# Revit family: Shower-Drain-KOHLER-Round-K-9132
name_source: partatom
category: Specialty Equipment
revit_build: Autodesk Revit 2015 (Build: 20140606_1530(x64)
units: mm (PartAtom-declared; Revit-internal decimal feet)

## types (12) — shared parameters
ADA = No
Assembly Code = C1030200
Date Modified = 02/28/2018
Default Elevation = 42"
Description = Round shower drain for use with plastic pipe, gasket included
Height = 1 15/16"
Length = 4 1/2"
Manufacturer = KOHLER Co.
MasterFormat 1995 = 10820
MasterFormat 2004 = 10.28.13
Material = Solid Brass Construction
Product Documentation Link = http://www.us.kohler.com
Product Name = Shower Drain
Product Page URL = http://www.us.kohler.com
URL = https://www.us.kohler.com
Width = 4 1/2"

## per-type parameters (varying)
| type | Finish | Model | Type |
| CP- Polished Chrome | Kohler-Metal-CP-Polished_Chrome | K-9132-CP | 1 |
| SN- Vibrant Polished Nickel | Kohler-Metal-SN-Vibrant_Polished_Nickel | K-9132-SN | 2 |
| AF- Vibrant French Gold | Kohler-Metal-AF-Vibrant_French_Gold | K-9132-AF | 3 |
| PB- Vibrant Polished Brass | Kohler-Metal-PB-Vibrant_Polished_Brass | K-9132-PB | 4 |
| BGD- Vibrant Moderne Brushed Gold | Kohler-Metal-BGD-Vibrant_Moderne_Brushed_Gold | K-9132-BGD | 5 |
| G- Brushed Chrome | Kohler-Metal-G-Brushed_Chrome | K-9132-G | 6 |
| BN- Vibrant Brushed Nickel | Kohler-Metal-BN-Vibrant_Brushed_Nickel | K-9132-BN | 7 |
| BV- Vibrant Brushed Bronze | Kohler-Metal-BV-Brushed_Bronze | K-9132-BV | 8 |
| 2BZ- Oil-Rubbed Bronze | Kohler-Metal-2BZ-Oil_Rubbed_Bronze | K-9132-2BZ | 9 |
| BL- Matte Black | Kohler-Metal-BL-Matte_Black | K-9132-BL | 10 |
| TT- Titanium | Kohler-Metal-TT-Vibrant_Titanium | K-9132-TT | 11 |
| VNT- Vintage Nickel | Kohler-Metal-VNT-Vintage_Nickel | K-9132-VNT | 12 |

## geometry (parser evidence)
native form markers: Sweep x5
no freeform markers — native parametric forms only
